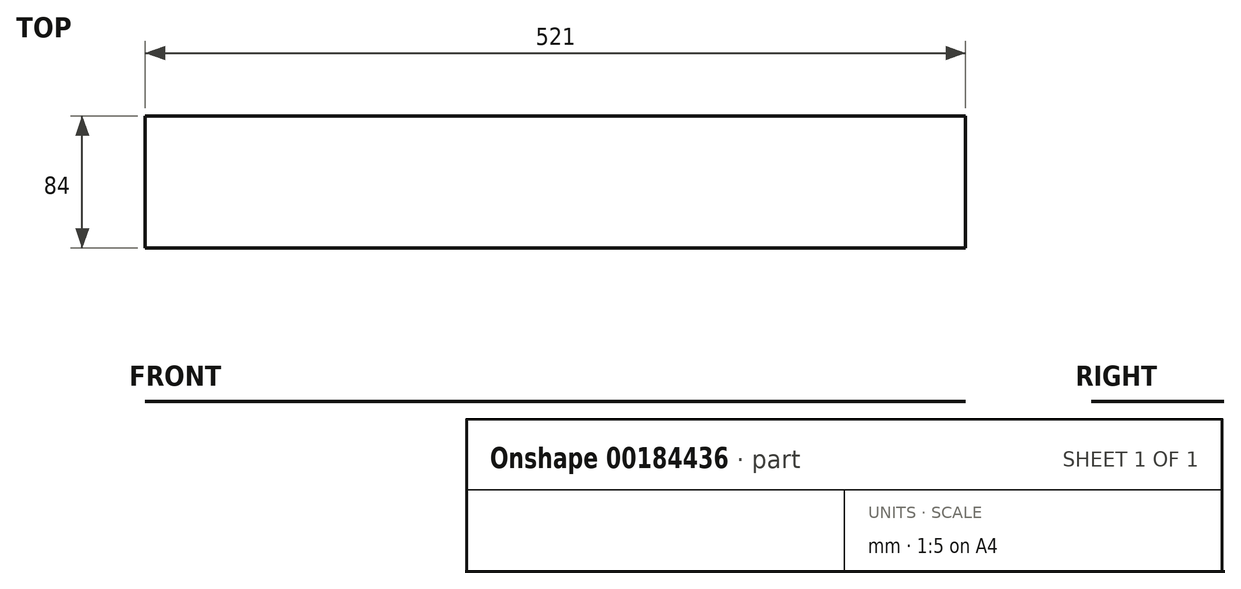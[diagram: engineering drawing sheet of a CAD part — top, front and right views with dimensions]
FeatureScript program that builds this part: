
annotation { "Feature Type Name" : "Feature", "Feature Type Description" : "" }
export const myFeature = defineFeature(function(context is Context, id is Id, definition is map)
    precondition{}
    {
        {
            var Q0;
            Q0=qCreatedBy(makeId("Top.planeOp"),FACE);
            var sketch = newSketch(context, id + "F0", { "sketchPlane" : qUnion([Q0])});
            skLineSegment(sketch, "E0.bottom", {"start": v(-260.5, 42) * mm, "end": v(260.5, 42) * mm});
            skLineSegment(sketch, "E0.top", {"start": v(-260.5, -42) * mm, "end": v(260.5, -42) * mm});
            skLineSegment(sketch, "E0.left", {"start": v(-260.5, 42) * mm, "end": v(-260.5, -42) * mm});
            skLineSegment(sketch, "E0.right", {"start": v(260.5, 42) * mm, "end": v(260.5, -42) * mm});
            skPoint(sketch, "E0.middle", {"position": v(0, 0) * mm});
            skSolve(sketch);
        }
        {
            var Q0;
            Q0=makeQuery(id+"F0.imprint","IMPRINT",FACE,{"disambiguationData":[TD([[makeQuery(id+"F0.imprint","IMPRINT",EDGE,{"derivedFrom":sQuery(id+"F0.wireOp",EDGE,"E0.bottom")}),-1.0]])]});
            extrude(context, id + "F1", {"entities" : qUnion([Q0]), "depth" : 1 / 203.2 * mm});
        }
    });
